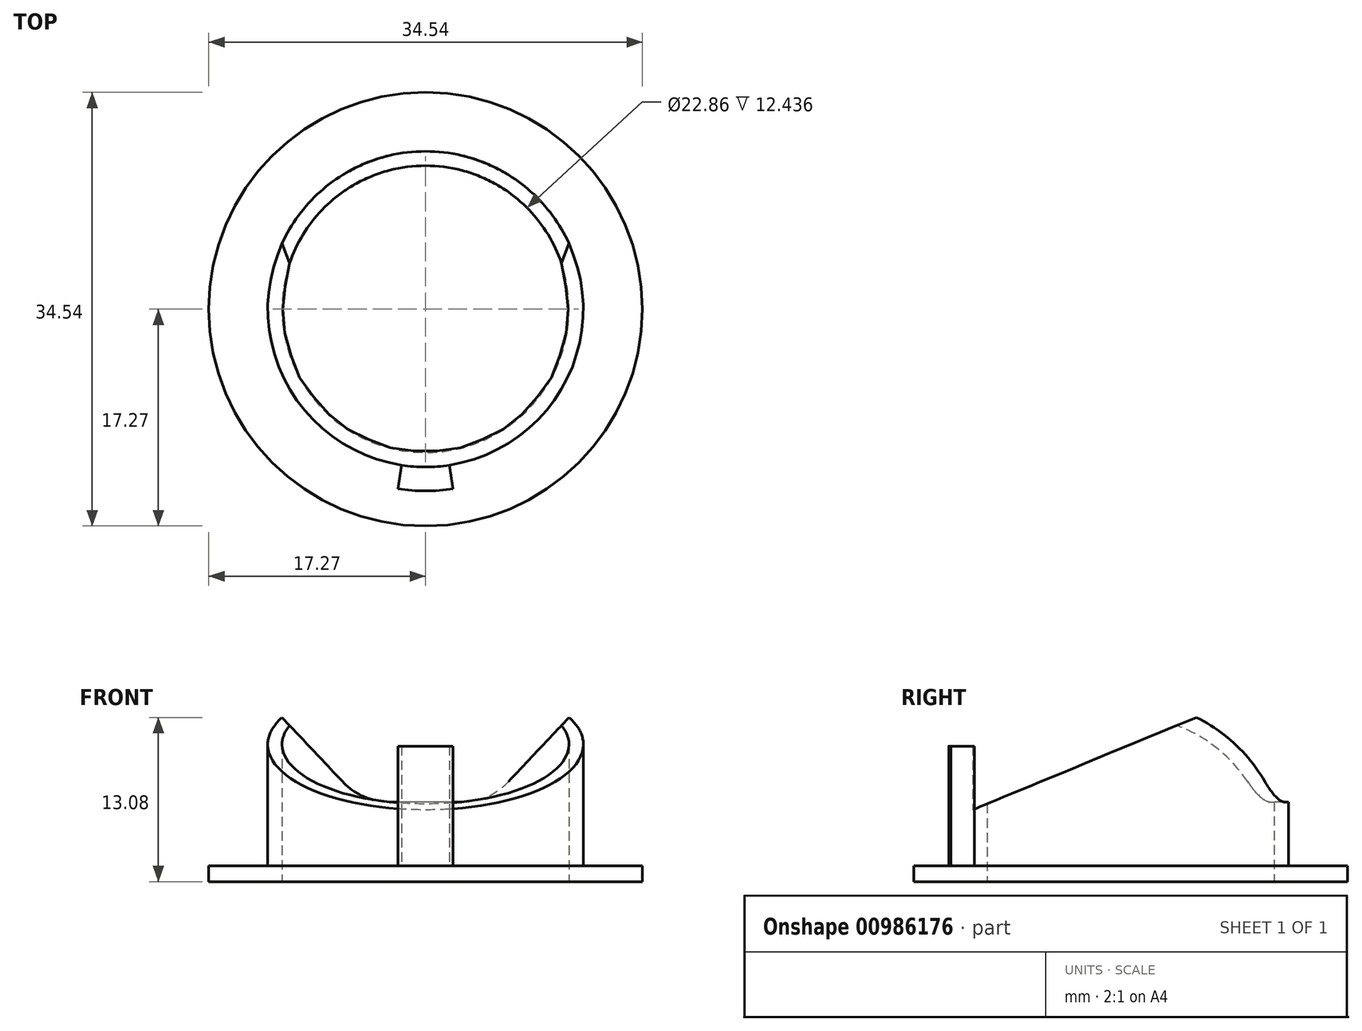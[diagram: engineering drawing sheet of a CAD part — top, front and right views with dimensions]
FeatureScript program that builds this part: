
annotation { "Feature Type Name" : "Feature", "Feature Type Description" : "" }
export const myFeature = defineFeature(function(context is Context, id is Id, definition is map)
    precondition{}
    {
        {
            var Q0;
            Q0=qCreatedBy(makeId("Top.planeOp"),FACE);
            var sketch = newSketch(context, id + "F0", { "sketchPlane" : qUnion([Q0])});
            skCircle(sketch, "E0", {"center": v(0, 0) * mm, "radius": 17.27 * mm});
            skCircle(sketch, "E1", {"center": v(0, 0) * mm, "radius": 11.43 * mm});
            skSolve(sketch);
        }
        {
            var Q0;
            Q0 = qSketchRegion(id + "F0", true);
            extrude(context, id + "F1", {"entities" : qUnion([Q0]), "depth" : 1.27 * mm, "offsetDistance" : 25.4 * mm});
        }
        {
            var Q0;
            Q0=makeQuery(id+"F1.opExtrude","CAP_FACE",FACE,{"disambiguationData":[OSD([sQuery(id+"F0.wireOp",EDGE,"E0"),sQuery(id+"F0.wireOp",EDGE,"E1")])],"isStart":false});
            var sketch = newSketch(context, id + "F2", { "sketchPlane" : qUnion([Q0])});
            skCircle(sketch, "E2.0", {"center": v(0, 0) * mm, "radius": 11.43 * mm});
            skCircle(sketch, "E3", {"center": v(0, 0) * mm, "radius": 12.57 * mm});
            skSolve(sketch);
        }
        {
            var Q0;
            Q0 = qSketchRegion(id + "F2", true);
            extrude(context, id + "F3", {"entities" : qUnion([Q0]), "operationType" : NewBodyOperationType.ADD, "depth" : 11.8 * mm, "offsetDistance" : 25.4 * mm});
        }
        {
            var Q0;
            Q0=qCreatedBy(makeId("Front.planeOp"),FACE);
            var sketch = newSketch(context, id + "F4", { "sketchPlane" : qUnion([Q0])});
            skLineSegment(sketch, "E4.0", {"start": v(-12.57, 13.08) * mm, "end": v(-11.43, 13.08) * mm, "construction": true});
            skLineSegment(sketch, "E5.top", {"start": v(2.89, 6.35) * mm, "end": v(-2.89, 6.35) * mm});
            skPoint(sketch, "E6.visualSharp", {"position": v(2.72, 6.35) * mm});
            skPoint(sketch, "E7.visualSharp", {"position": v(-6.9, 9.59) * mm});
            skLineSegment(sketch, "E8", {"start": v(-6.58, 7.94) * mm, "end": v(-11.43, 13.08) * mm});
            skLineSegment(sketch, "E9", {"start": v(6.58, 7.94) * mm, "end": v(11.43, 13.08) * mm});
            skLineSegment(sketch, "E10", {"start": v(-12.57, 1.27) * mm, "end": v(-12.57, 13.08) * mm, "construction": true});
            skLineSegment(sketch, "E11.trimOffspring", {"start": v(11.43, 13.08) * mm, "end": v(12.57, 13.08) * mm, "construction": true});
            skLineSegment(sketch, "E12", {"start": v(-11.43, 13.08) * mm, "end": v(11.43, 13.08) * mm});
            skPoint(sketch, "E13.visualSharp", {"position": v(-5.08, 6.35) * mm});
            skArc(sketch, "E13.filletArc", {"start": v(-6.58, 7.94) * mm, "mid": v(-4.9, 6.77) * mm, "end": v(-2.89, 6.35) * mm});
            skPoint(sketch, "E14.visualSharp", {"position": v(5.08, 6.35) * mm});
            skArc(sketch, "E14.filletArc", {"start": v(2.89, 6.35) * mm, "mid": v(4.9, 6.77) * mm, "end": v(6.58, 7.94) * mm});
            skSolve(sketch);
        }
        {
            var Q0;
            Q0 = qSketchRegion(id + "F4", true);
            extrude(context, id + "F5", {"entities" : qUnion([Q0]), "operationType" : NewBodyOperationType.REMOVE, "endBound" : BoundingType.THROUGH_ALL, "oppositeDirection" : true, "depth" : 25.4 * mm, "offsetDistance" : 25.4 * mm});
        }
        {
            var Q0;
            Q0=qCreatedBy(makeId("Right.planeOp"),FACE);
            var sketch = newSketch(context, id + "F6", { "sketchPlane" : qUnion([Q0])});
            skLineSegment(sketch, "E15", {"start": v(12.57, 5.72) * mm, "end": v(12.57, 3.18) * mm, "construction": true});
            skLineSegment(sketch, "E16.0", {"start": v(5.24, 13.08) * mm, "end": v(-12.57, 13.08) * mm});
            skLineSegment(sketch, "E17", {"start": v(-12.57, 5.72) * mm, "end": v(-12.57, 13.08) * mm});
            skLineSegment(sketch, "E18", {"start": v(12.57, 5.72) * mm, "end": v(-12.57, 5.72) * mm, "construction": true});
            skLineSegment(sketch, "E19", {"start": v(5.24, 13.08) * mm, "end": v(-12.57, 5.72) * mm});
            skSolve(sketch);
        }
        {
            var Q0;
            Q0 = qSketchRegion(id + "F6", true);
            extrude(context, id + "F7", {"entities" : qUnion([Q0]), "operationType" : NewBodyOperationType.REMOVE, "endBound" : BoundingType.SYMMETRIC, "depth" : 25.4 * mm, "offsetDistance" : 25.4 * mm});
        }
        {
            var Q0;
            Q0=makeQuery(id+"F1.opExtrude","CAP_FACE",FACE,{"disambiguationData":[OSD([sQuery(id+"F0.wireOp",EDGE,"E0"),sQuery(id+"F0.wireOp",EDGE,"E1")])],"isStart":false});
            var sketch = newSketch(context, id + "F8", { "sketchPlane" : qUnion([Q0])});
            skArc(sketch, "E20", {"start": v(1.9, -12.43) * mm, "mid": v(0, -12.57) * mm, "end": v(-1.9, -12.43) * mm});
            skLineSegment(sketch, "E21", {"start": v(-1.9, -12.43) * mm, "end": v(1.9, -12.43) * mm, "construction": true});
            skLineSegment(sketch, "E22", {"start": v(-1.9, -12.43) * mm, "end": v(-2.2, -14.31) * mm});
            skLineSegment(sketch, "E23", {"start": v(1.9, -12.43) * mm, "end": v(2.2, -14.31) * mm});
            skLineSegment(sketch, "E24", {"start": v(1.9, -12.43) * mm, "end": v(0, 0) * mm, "construction": true});
            skArc(sketch, "E25", {"start": v(2.2, -14.31) * mm, "mid": v(0, -14.48) * mm, "end": v(-2.2, -14.31) * mm});
            skSolve(sketch);
        }
        {
            var Q0;
            Q0 = qSketchRegion(id + "F8", true);
            extrude(context, id + "F9", {"entities" : qUnion([Q0]), "operationType" : NewBodyOperationType.ADD, "depth" : 9.52 * mm, "offsetDistance" : 25.4 * mm});
        }
    });
